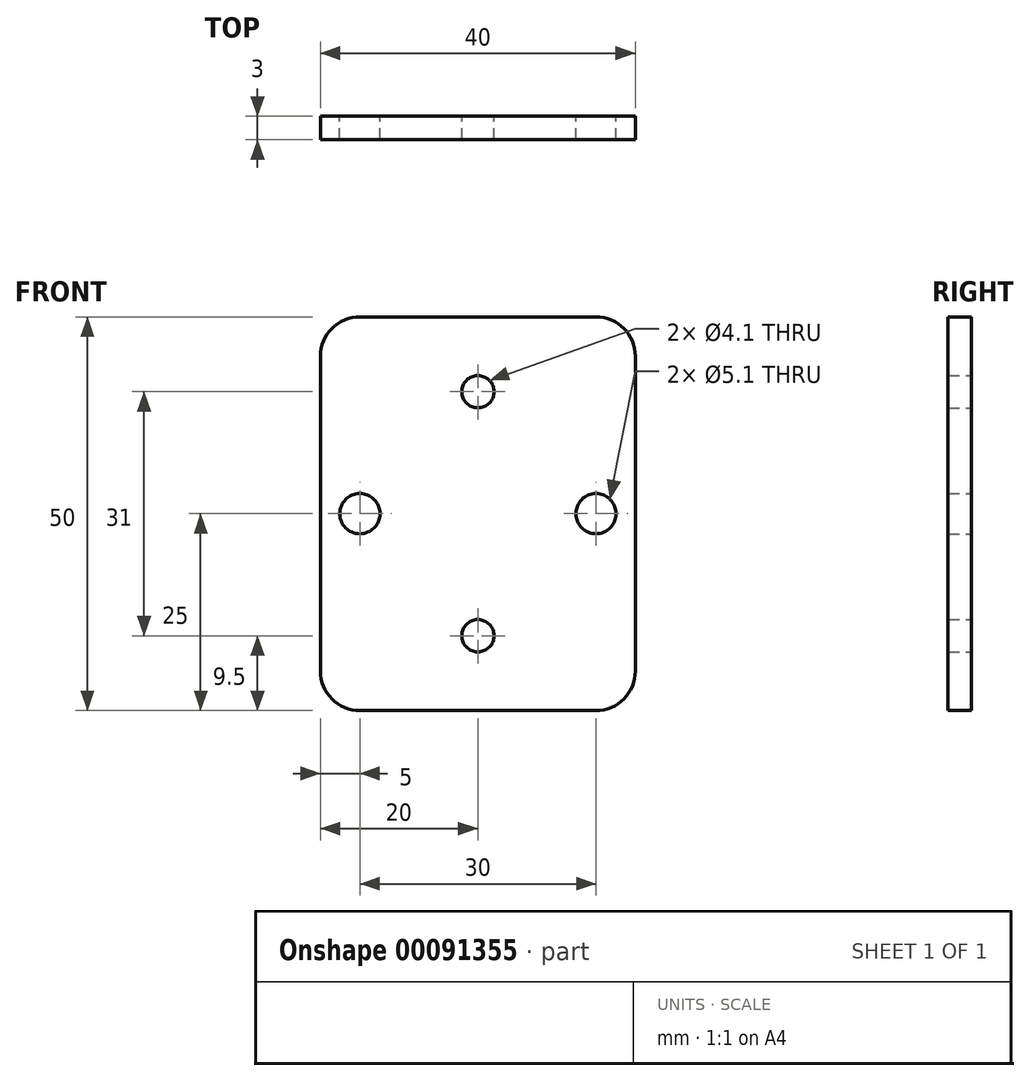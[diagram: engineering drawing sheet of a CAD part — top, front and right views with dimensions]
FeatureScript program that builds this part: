
annotation { "Feature Type Name" : "Feature", "Feature Type Description" : "" }
export const myFeature = defineFeature(function(context is Context, id is Id, definition is map)
    precondition{}
    {
        {
            var Q0;
            Q0=qCreatedBy(makeId("Front.planeOp"),FACE);
            var sketch = newSketch(context, id + "F0", { "sketchPlane" : qUnion([Q0])});
            skLineSegment(sketch, "E0", {"start": v(0, 66.43) * mm, "end": v(0, -63.57) * mm, "construction": true});
            skLineSegment(sketch, "E1", {"start": v(-51.14, 0) * mm, "end": v(50.57, 0) * mm, "construction": true});
            skLineSegment(sketch, "E2.bottom", {"start": v(-20, -25) * mm, "end": v(20, -25) * mm});
            skLineSegment(sketch, "E2.top", {"start": v(-20, 25) * mm, "end": v(20, 25) * mm});
            skLineSegment(sketch, "E2.left", {"start": v(-20, -25) * mm, "end": v(-20, 25) * mm});
            skLineSegment(sketch, "E2.right", {"start": v(20, -25) * mm, "end": v(20, 25) * mm});
            skSolve(sketch);
        }
        {
            var Q0;
            Q0=makeQuery(id+"F0.imprint","IMPRINT",FACE,{"disambiguationData":[TD([[makeQuery(id+"F0.imprint","IMPRINT",EDGE,{"derivedFrom":sQuery(id+"F0.wireOp",EDGE,"E2.bottom")}),1.0]])]});
            extrude(context, id + "F1", {"entities" : qUnion([Q0]), "oppositeDirection" : true, "depth" : 3 * mm});
        }
        {
            var Q0;
            Q0=makeQuery(id+"F1.opExtrude","CAP_FACE",FACE,{"disambiguationData":[OSD([sQuery(id+"F0.wireOp",EDGE,"E2.bottom"),sQuery(id+"F0.wireOp",EDGE,"E2.top"),sQuery(id+"F0.wireOp",EDGE,"E2.left"),sQuery(id+"F0.wireOp",EDGE,"E2.right")])],"isStart":true});
            var sketch = newSketch(context, id + "F2", { "sketchPlane" : qUnion([Q0])});
            skLineSegment(sketch, "E3", {"start": v(0, 25) * mm, "end": v(0, -25) * mm, "construction": true});
            skLineSegment(sketch, "E4", {"start": v(-20, 0) * mm, "end": v(20, 0) * mm, "construction": true});
            skPoint(sketch, "E5", {"position": v(0, 15.5) * mm});
            skPoint(sketch, "E6", {"position": v(0, -15.5) * mm});
            skPoint(sketch, "E7", {"position": v(-15, 0) * mm});
            skPoint(sketch, "E8", {"position": v(15, 0) * mm});
            skSolve(sketch);
        }
        {
            var Q0;
            Q0=sQuery(id+"F2.wireOp",VERTEX,"E5");
            var Q1;
            Q1=sQuery(id+"F2.wireOp",VERTEX,"E6");
            var Q2;
            Q2=makeQuery(id+"F1.opExtrude","SWEPT_BODY",BODY,{"disambiguationData":[OSD([sQuery(id+"F0.wireOp",EDGE,"E2.bottom"),sQuery(id+"F0.wireOp",EDGE,"E2.top"),sQuery(id+"F0.wireOp",EDGE,"E2.left"),sQuery(id+"F0.wireOp",EDGE,"E2.right")])]});
            hole(context, id + "F3", {"style" : HoleStyle.SIMPLE, "endStyle" : HoleEndStyle.THROUGH, "standardTappedOrClearance" : lookupTablePath({ "standard" : "ISO", "engagement" : "75%", "pitch" : "0.9 mm", "size" : "M5", "type" : "Tapped" }), "standardBlindInLast" : lookupTablePath({ "standard" : "ISO", "engagement" : "75%", "pitch" : "0.9 mm", "size" : "M5", "type" : "Tapped" }), "holeDiameter" : 4.1 * mm, "locations" : qUnion([Q0, Q1]), "scope" : qUnion([Q2]), "isTappedThrough" : true, "showTappedDepth" : true, "startStyle" : HoleStartStyle.SKETCH});
        }
        {
            var Q0;
            Q0=sQuery(id+"F2.wireOp",VERTEX,"E7");
            var Q1;
            Q1=sQuery(id+"F2.wireOp",VERTEX,"E8");
            var Q2;
            Q2=makeQuery(id+"F1.opExtrude","SWEPT_BODY",BODY,{"disambiguationData":[OSD([sQuery(id+"F0.wireOp",EDGE,"E2.bottom"),sQuery(id+"F0.wireOp",EDGE,"E2.top"),sQuery(id+"F0.wireOp",EDGE,"E2.left"),sQuery(id+"F0.wireOp",EDGE,"E2.right")])]});
            hole(context, id + "F4", {"style" : HoleStyle.SIMPLE, "endStyle" : HoleEndStyle.THROUGH, "standardTappedOrClearance" : lookupTablePath({ "standard" : "ISO", "size" : "5.1", "type" : "Drilled" }), "standardBlindInLast" : lookupTablePath({ "standard" : "ISO", "size" : "5.1", "type" : "Drilled" }), "holeDiameter" : 5.1 * mm, "locations" : qUnion([Q0, Q1]), "scope" : qUnion([Q2]), "isTappedThrough" : true, "startStyle" : HoleStartStyle.SKETCH});
        }
        {
            var Q0;
            Q0=makeQuery(id+"F1.opExtrude","SWEPT_EDGE",EDGE,{"disambiguationData":[OSD([sQuery(id+"F0.wireOp",EDGE,"E2.top"),sQuery(id+"F0.wireOp",EDGE,"E2.right")])]});
            var Q1;
            Q1=makeQuery(id+"F1.opExtrude","SWEPT_EDGE",EDGE,{"disambiguationData":[OSD([sQuery(id+"F0.wireOp",EDGE,"E2.bottom"),sQuery(id+"F0.wireOp",EDGE,"E2.right")])]});
            var Q2;
            Q2=makeQuery(id+"F1.opExtrude","SWEPT_EDGE",EDGE,{"disambiguationData":[OSD([sQuery(id+"F0.wireOp",EDGE,"E2.bottom"),sQuery(id+"F0.wireOp",EDGE,"E2.left")])]});
            var Q3;
            Q3=makeQuery(id+"F1.opExtrude","SWEPT_EDGE",EDGE,{"disambiguationData":[OSD([sQuery(id+"F0.wireOp",EDGE,"E2.top"),sQuery(id+"F0.wireOp",EDGE,"E2.left")])]});
            fillet(context, id + "F5", {"entities" : qUnion([Q0, Q1, Q2, Q3]), "radius" : 5 * mm, "tangentPropagation" : true, "allowEdgeOverflow" : false});
        }
    });
